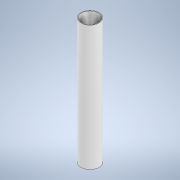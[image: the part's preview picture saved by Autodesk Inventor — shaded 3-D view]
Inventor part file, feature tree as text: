
AUTODESK INVENTOR PART (.ipt)
format: ipt  version: 2022 (Build 260153000, 153)  size: 96,768 bytes
history: native  units: mm
features: extrude x1, sketch x1
ambient origin geometry x8: Origin, YZ Plane, XZ Plane, XY Plane, X Axis, Y Axis, Z Axis, Center Point
bodies: Solid1 (feature_tree)
feature tree (2):
  extrude  "Extrusion1"  Depth=200.0mm
  sketch  "Sketch1"  dims[d0=29.0mm d1=27.0mm d2=200.0mm d3=0.0mm]
